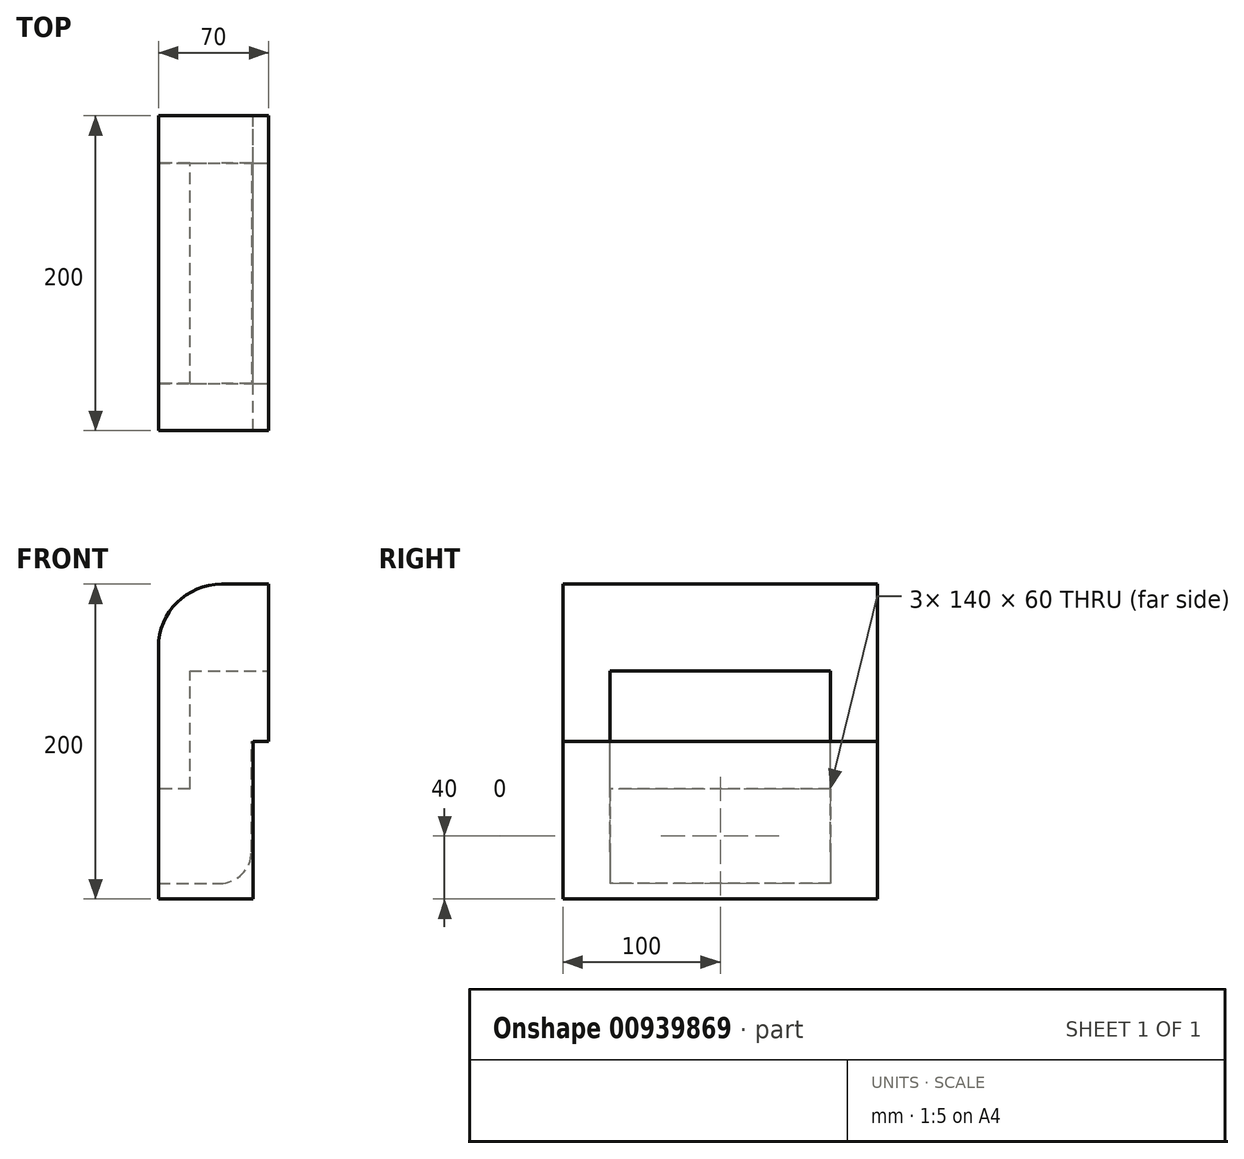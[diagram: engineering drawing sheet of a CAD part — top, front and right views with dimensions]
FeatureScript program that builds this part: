
annotation { "Feature Type Name" : "Feature", "Feature Type Description" : "" }
export const myFeature = defineFeature(function(context is Context, id is Id, definition is map)
    precondition{}
    {
        {
            var Q0;
            Q0=qCreatedBy(makeId("Right.planeOp"),FACE);
            var sketch = newSketch(context, id + "F0", { "sketchPlane" : qUnion([Q0])});
            skLineSegment(sketch, "E0.bottom", {"start": v(-100, 100) * mm, "end": v(100, 100) * mm});
            skLineSegment(sketch, "E0.top", {"start": v(-100, -100) * mm, "end": v(100, -100) * mm});
            skLineSegment(sketch, "E0.left", {"start": v(-100, 100) * mm, "end": v(-100, -100) * mm});
            skLineSegment(sketch, "E0.right", {"start": v(100, 100) * mm, "end": v(100, -100) * mm});
            skPoint(sketch, "E0.middle", {"position": v(0, 0) * mm});
            skSolve(sketch);
        }
        {
            var Q0;
            Q0 = qSketchRegion(id + "F0", true);
            extrude(context, id + "F1", {"entities" : qUnion([Q0]), "oppositeDirection" : true, "depth" : 70 * mm, "offsetDistance" : 25 * mm});
        }
        {
            var Q0;
            Q0=makeQuery(id+"F1.opExtrude","SWEPT_FACE",FACE,{"disambiguationData":[OSD([sQuery(id+"F0.wireOp",EDGE,"E0.top")])]});
            var sketch = newSketch(context, id + "F2", { "sketchPlane" : qUnion([Q0])});
            skLineSegment(sketch, "E1.bottom", {"start": v(0, 100) * mm, "end": v(-10, 100) * mm});
            skLineSegment(sketch, "E1.top", {"start": v(0, -100) * mm, "end": v(-10, -100) * mm});
            skLineSegment(sketch, "E1.left", {"start": v(0, 100) * mm, "end": v(0, -100) * mm});
            skLineSegment(sketch, "E1.right", {"start": v(-10, 100) * mm, "end": v(-10, -100) * mm});
            skSolve(sketch);
        }
        {
            var Q0;
            Q0 = qSketchRegion(id + "F2", true);
            extrude(context, id + "F3", {"entities" : qUnion([Q0]), "operationType" : NewBodyOperationType.REMOVE, "oppositeDirection" : true, "depth" : 100 * mm, "offsetDistance" : 25 * mm});
        }
        {
            var Q0;
            Q0=makeQuery(id+"F1.opExtrude","CAP_FACE",FACE,{"disambiguationData":[OSD([sQuery(id+"F0.wireOp",EDGE,"E0.bottom"),sQuery(id+"F0.wireOp",EDGE,"E0.top"),sQuery(id+"F0.wireOp",EDGE,"E0.left"),sQuery(id+"F0.wireOp",EDGE,"E0.right")])],"isStart":true});
            var sketch = newSketch(context, id + "F4", { "sketchPlane" : qUnion([Q0])});
            skLineSegment(sketch, "E2.bottom", {"start": v(-70, 0) * mm, "end": v(70, 0) * mm});
            skLineSegment(sketch, "E2.top", {"start": v(-70, 45) * mm, "end": v(70, 45) * mm});
            skLineSegment(sketch, "E2.left", {"start": v(-70, 0) * mm, "end": v(-70, 45) * mm});
            skLineSegment(sketch, "E2.right", {"start": v(70, 0) * mm, "end": v(70, 45) * mm});
            skSolve(sketch);
        }
        {
            var Q0;
            Q0 = qSketchRegion(id + "F4", true);
            extrude(context, id + "F5", {"entities" : qUnion([Q0]), "operationType" : NewBodyOperationType.REMOVE, "oppositeDirection" : true, "depth" : 50 * mm, "offsetDistance" : 25 * mm});
        }
        {
            var Q0;
            Q0=makeQuery(id+"F5.boolean.opBoolean","COPY",FACE,{"derivedFrom":makeQuery(id+"F5.opExtrude","SWEPT_FACE",FACE,{"disambiguationData":[OSD([sQuery(id+"F4.wireOp",EDGE,"E2.bottom")])]})});
            var sketch = newSketch(context, id + "F6", { "sketchPlane" : qUnion([Q0])});
            skLineSegment(sketch, "E3.bottom", {"start": v(-50, 70) * mm, "end": v(-11, 70) * mm});
            skLineSegment(sketch, "E3.top", {"start": v(-50, -70) * mm, "end": v(-11, -70) * mm});
            skLineSegment(sketch, "E3.left", {"start": v(-50, 70) * mm, "end": v(-50, -70) * mm});
            skLineSegment(sketch, "E3.right", {"start": v(-11, 70) * mm, "end": v(-11, -70) * mm});
            skSolve(sketch);
        }
        {
            var Q0;
            Q0=makeQuery(id+"F6.imprint","IMPRINT",FACE,{"disambiguationData":[TD([[makeQuery(id+"F6.imprint","IMPRINT",EDGE,{"derivedFrom":sQuery(id+"F6.wireOp",EDGE,"E3.bottom")}),-1.0]])]});
            extrude(context, id + "F7", {"entities" : qUnion([Q0]), "operationType" : NewBodyOperationType.REMOVE, "oppositeDirection" : true, "depth" : 90 * mm, "offsetDistance" : 25 * mm});
        }
        {
            var Q0;
            Q0=makeQuery(id+"F1.opExtrude","CAP_FACE",FACE,{"disambiguationData":[OSD([sQuery(id+"F0.wireOp",EDGE,"E0.bottom"),sQuery(id+"F0.wireOp",EDGE,"E0.top"),sQuery(id+"F0.wireOp",EDGE,"E0.left"),sQuery(id+"F0.wireOp",EDGE,"E0.right")])],"isStart":false});
            var sketch = newSketch(context, id + "F8", { "sketchPlane" : qUnion([Q0])});
            skLineSegment(sketch, "E4.bottom", {"start": v(-70, -30) * mm, "end": v(70, -30) * mm});
            skLineSegment(sketch, "E4.top", {"start": v(-70, -90) * mm, "end": v(70, -90) * mm});
            skLineSegment(sketch, "E4.left", {"start": v(-70, -30) * mm, "end": v(-70, -90) * mm});
            skLineSegment(sketch, "E4.right", {"start": v(70, -30) * mm, "end": v(70, -90) * mm});
            skSolve(sketch);
        }
        {
            var Q0;
            Q0 = qSketchRegion(id + "F8", true);
            extrude(context, id + "F9", {"entities" : qUnion([Q0]), "operationType" : NewBodyOperationType.REMOVE, "oppositeDirection" : true, "depth" : 59 * mm, "offsetDistance" : 25 * mm});
        }
        {
            var Q0;
            Q0=makeQuery(id+"F7.boolean.opBoolean","COPY",EDGE,{"derivedFrom":makeQuery(id+"F7.opExtrude","CAP_EDGE",EDGE,{"disambiguationData":[OSD([sQuery(id+"F6.wireOp",EDGE,"E3.right")])],"isStart":false})});
            fillet(context, id + "F10", {"entities" : qUnion([Q0]), "radius" : 20 * mm, "tangentPropagation" : true, "allowEdgeOverflow" : false});
        }
        {
            var Q0;
            Q0=makeQuery(id+"F1.opExtrude","CAP_EDGE",EDGE,{"disambiguationData":[OSD([sQuery(id+"F0.wireOp",EDGE,"E0.bottom")])],"isStart":false});
            fillet(context, id + "F11", {"entities" : qUnion([Q0]), "radius" : 40 * mm, "tangentPropagation" : true, "allowEdgeOverflow" : false});
        }
    });
